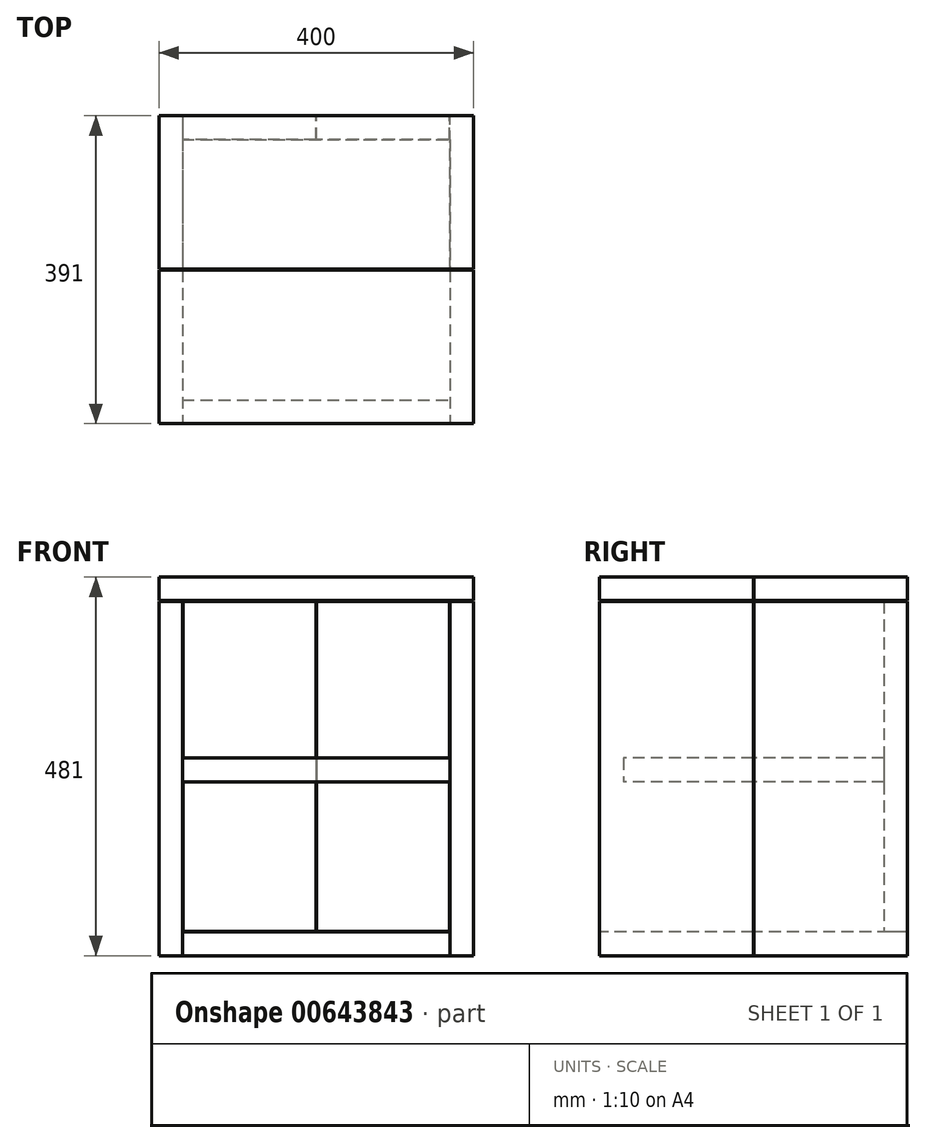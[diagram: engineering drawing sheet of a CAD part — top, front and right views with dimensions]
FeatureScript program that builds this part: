
annotation { "Feature Type Name" : "Feature", "Feature Type Description" : "" }
export const myFeature = defineFeature(function(context is Context, id is Id, definition is map)
    precondition{}
    {
        {
            var Q0;
            Q0=qCreatedBy(makeId("Right.planeOp"),FACE);
            var sketch = newSketch(context, id + "F0", { "sketchPlane" : qUnion([Q0])});
            skLineSegment(sketch, "E0.bottom", {"start": v(-219.17, 119.83) * mm, "end": v(-24.17, 119.83) * mm});
            skLineSegment(sketch, "E0.top", {"start": v(-219.17, 89.83) * mm, "end": v(-24.17, 89.83) * mm});
            skLineSegment(sketch, "E0.left", {"start": v(-219.17, 119.83) * mm, "end": v(-219.17, 89.83) * mm});
            skLineSegment(sketch, "E0.right", {"start": v(-24.17, 119.83) * mm, "end": v(-24.17, 89.83) * mm});
            skLineSegment(sketch, "E1.bottom", {"start": v(-23.17, 119.83) * mm, "end": v(171.83, 119.83) * mm});
            skLineSegment(sketch, "E1.top", {"start": v(-23.17, 89.83) * mm, "end": v(171.83, 89.83) * mm});
            skLineSegment(sketch, "E1.left", {"start": v(-23.17, 119.83) * mm, "end": v(-23.17, 89.83) * mm});
            skLineSegment(sketch, "E1.right", {"start": v(171.83, 119.83) * mm, "end": v(171.83, 89.83) * mm});
            skSolve(sketch);
        }
        {
            var Q0;
            Q0=makeQuery(id+"F0.imprint","IMPRINT",FACE,{"disambiguationData":[TD([[makeQuery(id+"F0.imprint","IMPRINT",EDGE,{"derivedFrom":sQuery(id+"F0.wireOp",EDGE,"E0.bottom")}),-1.0]])]});
            var Q1;
            Q1=makeQuery(id+"F0.imprint","IMPRINT",FACE,{"disambiguationData":[TD([[makeQuery(id+"F0.imprint","IMPRINT",EDGE,{"derivedFrom":sQuery(id+"F0.wireOp",EDGE,"E1.bottom")}),-1.0]])]});
            extrude(context, id + "F1", {"entities" : qUnion([Q0, Q1]), "endBound" : BoundingType.SYMMETRIC, "oppositeDirection" : true, "depth" : 400 * mm, "offsetDistance" : 25 * mm});
        }
        {
            var Q0;
            Q0=makeQuery(id+"F1.opExtrude","CAP_FACE",FACE,{"disambiguationData":[OSD([sQuery(id+"F0.wireOp",EDGE,"E0.bottom"),sQuery(id+"F0.wireOp",EDGE,"E0.top"),sQuery(id+"F0.wireOp",EDGE,"E0.left"),sQuery(id+"F0.wireOp",EDGE,"E0.right")])],"isStart":true});
            var sketch = newSketch(context, id + "F2", { "sketchPlane" : qUnion([Q0])});
            skLineSegment(sketch, "E2.bottom", {"start": v(-219.17, 88.83) * mm, "end": v(-24.17, 88.83) * mm});
            skLineSegment(sketch, "E2.top", {"start": v(-219.17, -361.17) * mm, "end": v(-24.17, -361.17) * mm});
            skLineSegment(sketch, "E2.left", {"start": v(-219.17, 88.83) * mm, "end": v(-219.17, -361.17) * mm});
            skLineSegment(sketch, "E2.right", {"start": v(-24.17, 88.83) * mm, "end": v(-24.17, -361.17) * mm});
            skLineSegment(sketch, "E3.bottom", {"start": v(-23.17, 88.83) * mm, "end": v(171.83, 88.83) * mm});
            skLineSegment(sketch, "E3.top", {"start": v(-23.17, -361.17) * mm, "end": v(171.83, -361.17) * mm});
            skLineSegment(sketch, "E3.left", {"start": v(-23.17, 88.83) * mm, "end": v(-23.17, -361.17) * mm});
            skLineSegment(sketch, "E3.right", {"start": v(171.83, 88.83) * mm, "end": v(171.83, -361.17) * mm});
            skSolve(sketch);
        }
        {
            var Q0;
            Q0 = qSketchRegion(id + "F2", true);
            extrude(context, id + "F3", {"entities" : qUnion([Q0]), "oppositeDirection" : true, "depth" : 30 * mm, "offsetDistance" : 25 * mm});
        }
        {
            var Q0;
            Q0=makeQuery(id+"F1.opExtrude","CAP_FACE",FACE,{"disambiguationData":[OSD([sQuery(id+"F0.wireOp",EDGE,"E0.bottom"),sQuery(id+"F0.wireOp",EDGE,"E0.top"),sQuery(id+"F0.wireOp",EDGE,"E0.left"),sQuery(id+"F0.wireOp",EDGE,"E0.right")])],"isStart":false});
            var sketch = newSketch(context, id + "F4", { "sketchPlane" : qUnion([Q0])});
            skLineSegment(sketch, "E4.bottom", {"start": v(-171.83, 88.83) * mm, "end": v(23.17, 88.83) * mm});
            skLineSegment(sketch, "E4.top", {"start": v(-171.83, -361.17) * mm, "end": v(23.17, -361.17) * mm});
            skLineSegment(sketch, "E4.left", {"start": v(-171.83, 88.83) * mm, "end": v(-171.83, -361.17) * mm});
            skLineSegment(sketch, "E4.right", {"start": v(23.17, 88.83) * mm, "end": v(23.17, -361.17) * mm});
            skLineSegment(sketch, "E5.bottom", {"start": v(24.17, 88.83) * mm, "end": v(219.17, 88.83) * mm});
            skLineSegment(sketch, "E5.top", {"start": v(24.17, -361.17) * mm, "end": v(219.17, -361.17) * mm});
            skLineSegment(sketch, "E5.left", {"start": v(24.17, 88.83) * mm, "end": v(24.17, -361.17) * mm});
            skLineSegment(sketch, "E5.right", {"start": v(219.17, 88.83) * mm, "end": v(219.17, -361.17) * mm});
            skSolve(sketch);
        }
        {
            var Q0;
            Q0 = qSketchRegion(id + "F4", true);
            extrude(context, id + "F5", {"entities" : qUnion([Q0]), "oppositeDirection" : true, "depth" : 30 * mm, "offsetDistance" : 25 * mm});
        }
        {
            var Q0;
            Q0=qCreatedBy(makeId("Right.planeOp"),FACE);
            var sketch = newSketch(context, id + "F6", { "sketchPlane" : qUnion([Q0])});
            skLineSegment(sketch, "E6.bottom", {"start": v(171.83, -361.17) * mm, "end": v(-23.17, -361.17) * mm});
            skLineSegment(sketch, "E6.top", {"start": v(171.83, -331.17) * mm, "end": v(-23.17, -331.17) * mm});
            skLineSegment(sketch, "E6.left", {"start": v(171.83, -361.17) * mm, "end": v(171.83, -331.17) * mm});
            skLineSegment(sketch, "E6.right", {"start": v(-23.17, -361.17) * mm, "end": v(-23.17, -331.17) * mm});
            skLineSegment(sketch, "E7.bottom", {"start": v(-24.17, -331.17) * mm, "end": v(-219.17, -331.17) * mm});
            skLineSegment(sketch, "E7.top", {"start": v(-24.17, -361.17) * mm, "end": v(-219.17, -361.17) * mm});
            skLineSegment(sketch, "E7.left", {"start": v(-24.17, -331.17) * mm, "end": v(-24.17, -361.17) * mm});
            skLineSegment(sketch, "E7.right", {"start": v(-219.17, -331.17) * mm, "end": v(-219.17, -361.17) * mm});
            skSolve(sketch);
        }
        {
            var Q0;
            Q0=makeQuery(id+"F6.imprint","IMPRINT",FACE,{"disambiguationData":[TD([[makeQuery(id+"F6.imprint","IMPRINT",EDGE,{"derivedFrom":sQuery(id+"F6.wireOp",EDGE,"E6.bottom")}),-1.0]])]});
            var Q1;
            Q1=makeQuery(id+"F6.imprint","IMPRINT",FACE,{"disambiguationData":[TD([[makeQuery(id+"F6.imprint","IMPRINT",EDGE,{"derivedFrom":sQuery(id+"F6.wireOp",EDGE,"E7.bottom")}),1.0]])]});
            extrude(context, id + "F7", {"entities" : qUnion([Q0, Q1]), "endBound" : BoundingType.SYMMETRIC, "oppositeDirection" : true, "depth" : 340 * mm, "offsetDistance" : 25 * mm});
        }
        {
            var Q0;
            Q0=makeQuery(id+"F7.opExtrude","SWEPT_FACE",FACE,{"disambiguationData":[OSD([sQuery(id+"F6.wireOp",EDGE,"E6.left")])]});
            var sketch = newSketch(context, id + "F8", { "sketchPlane" : qUnion([Q0])});
            skLineSegment(sketch, "E8.bottom", {"start": v(-169, 88.83) * mm, "end": v(-0.5, 88.83) * mm});
            skLineSegment(sketch, "E8.top", {"start": v(-169, -330.17) * mm, "end": v(-0.5, -330.17) * mm});
            skLineSegment(sketch, "E8.left", {"start": v(-169, 88.83) * mm, "end": v(-169, -330.17) * mm});
            skLineSegment(sketch, "E8.right", {"start": v(-0.5, 88.83) * mm, "end": v(-0.5, -330.17) * mm});
            skLineSegment(sketch, "E9.bottom", {"start": v(0.5, 88.83) * mm, "end": v(169, 88.83) * mm});
            skLineSegment(sketch, "E9.top", {"start": v(0.5, -330.17) * mm, "end": v(169, -330.17) * mm});
            skLineSegment(sketch, "E9.left", {"start": v(0.5, 88.83) * mm, "end": v(0.5, -330.17) * mm});
            skLineSegment(sketch, "E9.right", {"start": v(169, 88.83) * mm, "end": v(169, -330.17) * mm});
            skSolve(sketch);
        }
        {
            var Q0;
            Q0=makeQuery(id+"F8.imprint","IMPRINT",FACE,{"disambiguationData":[TD([[makeQuery(id+"F8.imprint","IMPRINT",EDGE,{"derivedFrom":sQuery(id+"F8.wireOp",EDGE,"E8.bottom")}),-1.0]])]});
            var Q1;
            Q1=makeQuery(id+"F8.imprint","IMPRINT",FACE,{"disambiguationData":[TD([[makeQuery(id+"F8.imprint","IMPRINT",EDGE,{"derivedFrom":sQuery(id+"F8.wireOp",EDGE,"E9.bottom")}),-1.0]])]});
            extrude(context, id + "F9", {"entities" : qUnion([Q0, Q1]), "oppositeDirection" : true, "depth" : 30 * mm, "offsetDistance" : 25 * mm});
        }
        {
            var Q0;
            Q0=makeQuery(id+"F3.opExtrude","CAP_FACE",FACE,{"disambiguationData":[OSD([sQuery(id+"F2.wireOp",EDGE,"E2.bottom"),sQuery(id+"F2.wireOp",EDGE,"E2.top"),sQuery(id+"F2.wireOp",EDGE,"E2.left"),sQuery(id+"F2.wireOp",EDGE,"E2.right")])],"isStart":false});
            var sketch = newSketch(context, id + "F10", { "sketchPlane" : qUnion([Q0])});
            skLineSegment(sketch, "E10.bottom", {"start": v(-141.83, -110.17) * mm, "end": v(23.17, -110.17) * mm});
            skLineSegment(sketch, "E10.top", {"start": v(-141.83, -140.17) * mm, "end": v(23.17, -140.17) * mm});
            skLineSegment(sketch, "E10.left", {"start": v(-141.83, -110.17) * mm, "end": v(-141.83, -140.17) * mm});
            skLineSegment(sketch, "E10.right", {"start": v(23.17, -110.17) * mm, "end": v(23.17, -140.17) * mm});
            skLineSegment(sketch, "E11.bottom", {"start": v(24.17, -110.17) * mm, "end": v(189.17, -110.17) * mm});
            skLineSegment(sketch, "E11.top", {"start": v(24.17, -140.17) * mm, "end": v(189.17, -140.17) * mm});
            skLineSegment(sketch, "E11.left", {"start": v(24.17, -110.17) * mm, "end": v(24.17, -140.17) * mm});
            skLineSegment(sketch, "E11.right", {"start": v(189.17, -110.17) * mm, "end": v(189.17, -140.17) * mm});
            skSolve(sketch);
        }
        {
            var Q0;
            Q0=makeQuery(id+"F10.imprint","IMPRINT",FACE,{"disambiguationData":[TD([[makeQuery(id+"F10.imprint","IMPRINT",EDGE,{"derivedFrom":sQuery(id+"F10.wireOp",EDGE,"E11.bottom")}),-1.0]])]});
            var Q1;
            Q1=makeQuery(id+"F10.imprint","IMPRINT",FACE,{"disambiguationData":[TD([[makeQuery(id+"F10.imprint","IMPRINT",EDGE,{"derivedFrom":sQuery(id+"F10.wireOp",EDGE,"E10.bottom")}),-1.0]])]});
            extrude(context, id + "F11", {"entities" : qUnion([Q0, Q1]), "depth" : 340 * mm, "offsetDistance" : 25 * mm});
        }
    });
